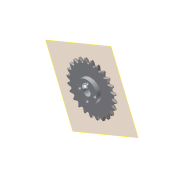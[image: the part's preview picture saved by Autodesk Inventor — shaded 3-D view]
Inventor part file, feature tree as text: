
AUTODESK INVENTOR PART (.ipt)
format: ipt  version: 2013 (Build 170138000, 138)  size: 789,504 bytes
history: native  units: in
note: dims shown in document units (in); Inventor stores cm internally (conversion verified against a paired STEP export)
features: imported_body x1, plane x1
ambient origin geometry x8: Origin, YZ Plane, XZ Plane, XY Plane, X Axis, Y Axis, Z Axis, Center Point
bodies: Solid1 (feature_tree)
feature tree (2):
  imported_body  "Base1"
  plane  "Work Plane1"
